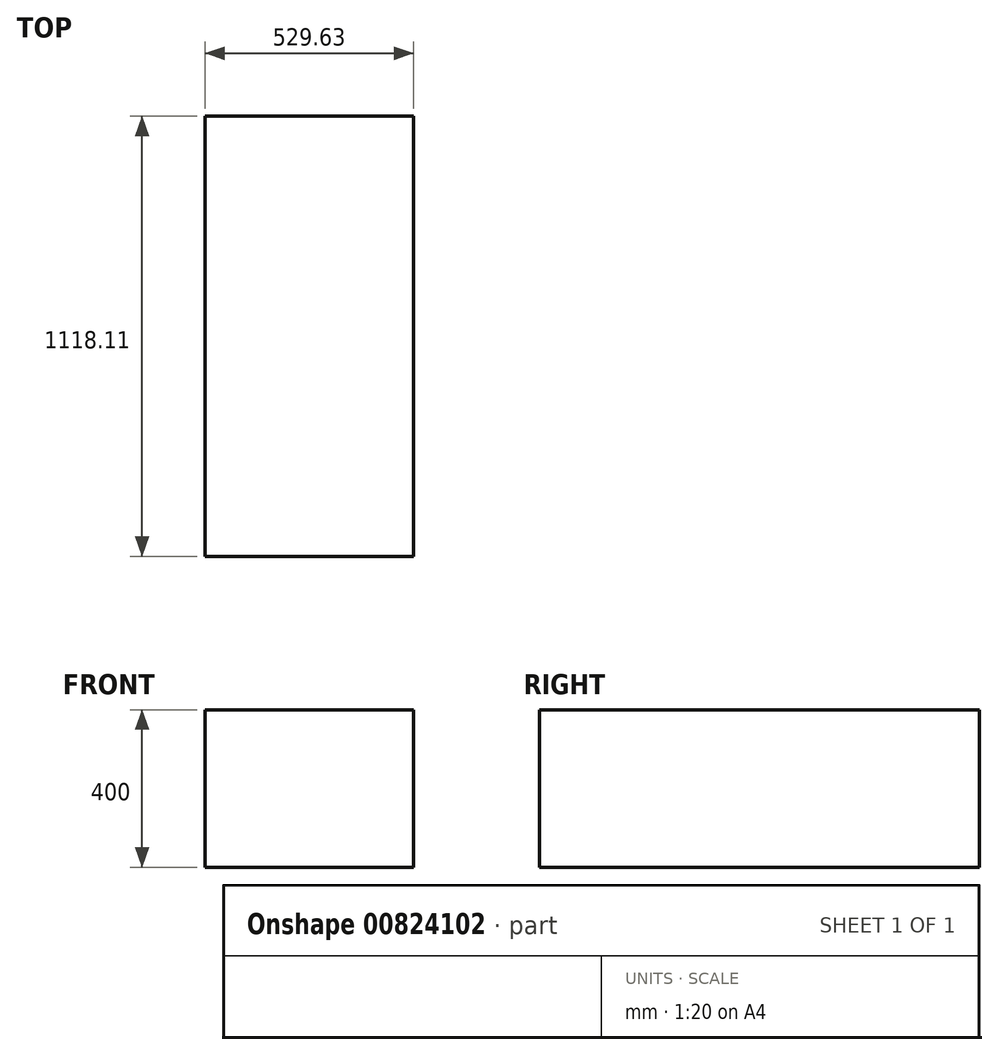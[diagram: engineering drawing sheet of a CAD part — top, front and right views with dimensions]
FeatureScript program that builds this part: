
annotation { "Feature Type Name" : "Feature", "Feature Type Description" : "" }
export const myFeature = defineFeature(function(context is Context, id is Id, definition is map)
    precondition{}
    {
        {
            var Q0;
            Q0=qCreatedBy(makeId("Top.planeOp"),FACE);
            var sketch = newSketch(context, id + "F0", { "sketchPlane" : qUnion([Q0])});
            skLineSegment(sketch, "E0.bottom", {"start": v(-869.44, 1886.32) * mm, "end": v(892.48, 1886.32) * mm});
            skLineSegment(sketch, "E0.top", {"start": v(-869.44, -1622) * mm, "end": v(892.48, -1622) * mm});
            skLineSegment(sketch, "E0.left", {"start": v(-869.44, 1886.32) * mm, "end": v(-869.44, -1622) * mm});
            skLineSegment(sketch, "E0.right", {"start": v(892.48, 1886.32) * mm, "end": v(892.48, -1622) * mm});
            skLineSegment(sketch, "E1", {"start": v(-865.23, 1891.8) * mm, "end": v(191.92, 1891.8) * mm});
            skLineSegment(sketch, "E2", {"start": v(191.92, 1891.8) * mm, "end": v(191.92, 1539.42) * mm});
            skLineSegment(sketch, "E3", {"start": v(191.92, 1539.42) * mm, "end": v(-630.3, 1539.42) * mm});
            skLineSegment(sketch, "E4", {"start": v(-630.3, 1539.42) * mm, "end": v(-630.3, 952.11) * mm});
            skLineSegment(sketch, "E5", {"start": v(-630.3, 952.11) * mm, "end": v(-865.23, 952.11) * mm});
            skLineSegment(sketch, "E6", {"start": v(-865.23, 952.11) * mm, "end": v(-865.23, 1891.8) * mm});
            skLineSegment(sketch, "E7.bottom", {"start": v(345.76, 438.3) * mm, "end": v(875.39, 438.3) * mm});
            skLineSegment(sketch, "E7.top", {"start": v(345.76, -679.8) * mm, "end": v(875.39, -679.8) * mm});
            skLineSegment(sketch, "E7.left", {"start": v(345.76, 438.3) * mm, "end": v(345.76, -679.8) * mm});
            skLineSegment(sketch, "E7.right", {"start": v(875.39, 438.3) * mm, "end": v(875.39, -679.8) * mm});
            skLineSegment(sketch, "E8", {"start": v(345.76, 179.24) * mm, "end": v(875.39, 179.24) * mm});
            skLineSegment(sketch, "E9", {"start": v(345.76, 179.24) * mm, "end": v(875.39, -120.76) * mm});
            skSolve(sketch);
        }
        {
            var Q0;
            {var subQ0=sQuery(id+"F0.wireOp",EDGE,"E7.top");Q0=makeQuery(id+"F0.imprint","IMPRINT",FACE,{"disambiguationData":[TD([[makeQuery(id+"F0.imprint","IMPRINT",EDGE,{"derivedFrom":subQ0}),1.0]])]});}
            var Q1;
            {var subQ0=sQuery(id+"F0.wireOp",EDGE,"E8");Q1=makeQuery(id+"F0.imprint","IMPRINT",FACE,{"disambiguationData":[TD([[makeQuery(id+"F0.imprint","IMPRINT",EDGE,{"derivedFrom":subQ0}),-1.0]])]});}
            var Q2;
            {var subQ0=sQuery(id+"F0.wireOp",EDGE,"E7.bottom");Q2=makeQuery(id+"F0.imprint","IMPRINT",FACE,{"disambiguationData":[TD([[makeQuery(id+"F0.imprint","IMPRINT",EDGE,{"derivedFrom":subQ0}),-1.0]])]});}
            extrude(context, id + "F1", {"entities" : qUnion([Q0, Q1, Q2]), "depth" : 400 * mm, "offsetDistance" : 25 * mm});
        }
    });
